# Revit family: Patio-Door_2900_Novatech
name_source: partatom
category: Doors
units: mm (PartAtom-declared; Revit-internal decimal feet)

## family parameters
Always vertical = Yes
Classification Number = 23.30.10.00
Cut with Voids When Loaded = No
Host = Wall
Room Calculation Point = No
Shared = No

## types (3) — shared parameters
Analytic Construction = <None>
CAD Details = https://www.arcat.com
Define Thermal Properties by = Schematic Type
Frame Material = Aluminum
Function = Interior
Handle Height = 38"
Hardware Material = Aluminum
Height = 80 3/8"
Height Sash O = 77 1/8"
Height Sash X = 77 1/8"
Keynote = 08 32 00
Look Handle = Yes
Manufacturer = Novatech
Model = 2900
Panel Material = Glass
Product Page URL = https://www.arcat.com
Rough Height = 80 7/8"
Specification = https://www.arcat.com
Thickness = 5 3/4"
URL = https://www.groupenovatech.com
View Handle = Yes
Wall Closure = By host

## per-type parameters (varying)
| type | Model_Sash to Reference Line | Rough Width | Width | Width Sash O | Width Sash X |
| 58 1/4"W X 80 3/8"H | 28 1/2" | 58 3/4" | 58 1/4" | 29 5/8" | 29 5/8" |
| 70 1/4"W X 80 3/8"H | 34 1/2" | 70 3/4" | 70 1/4" | 35 5/8" | 35 5/8" |
| 94 1/4"W X 80 3/8"H | 46 1/2" | 94 3/4" | 94 1/4" | 47 5/8" | 47 5/8" |

## geometry (parser evidence)
native form markers: Sweep x99
no freeform markers — native parametric forms only
